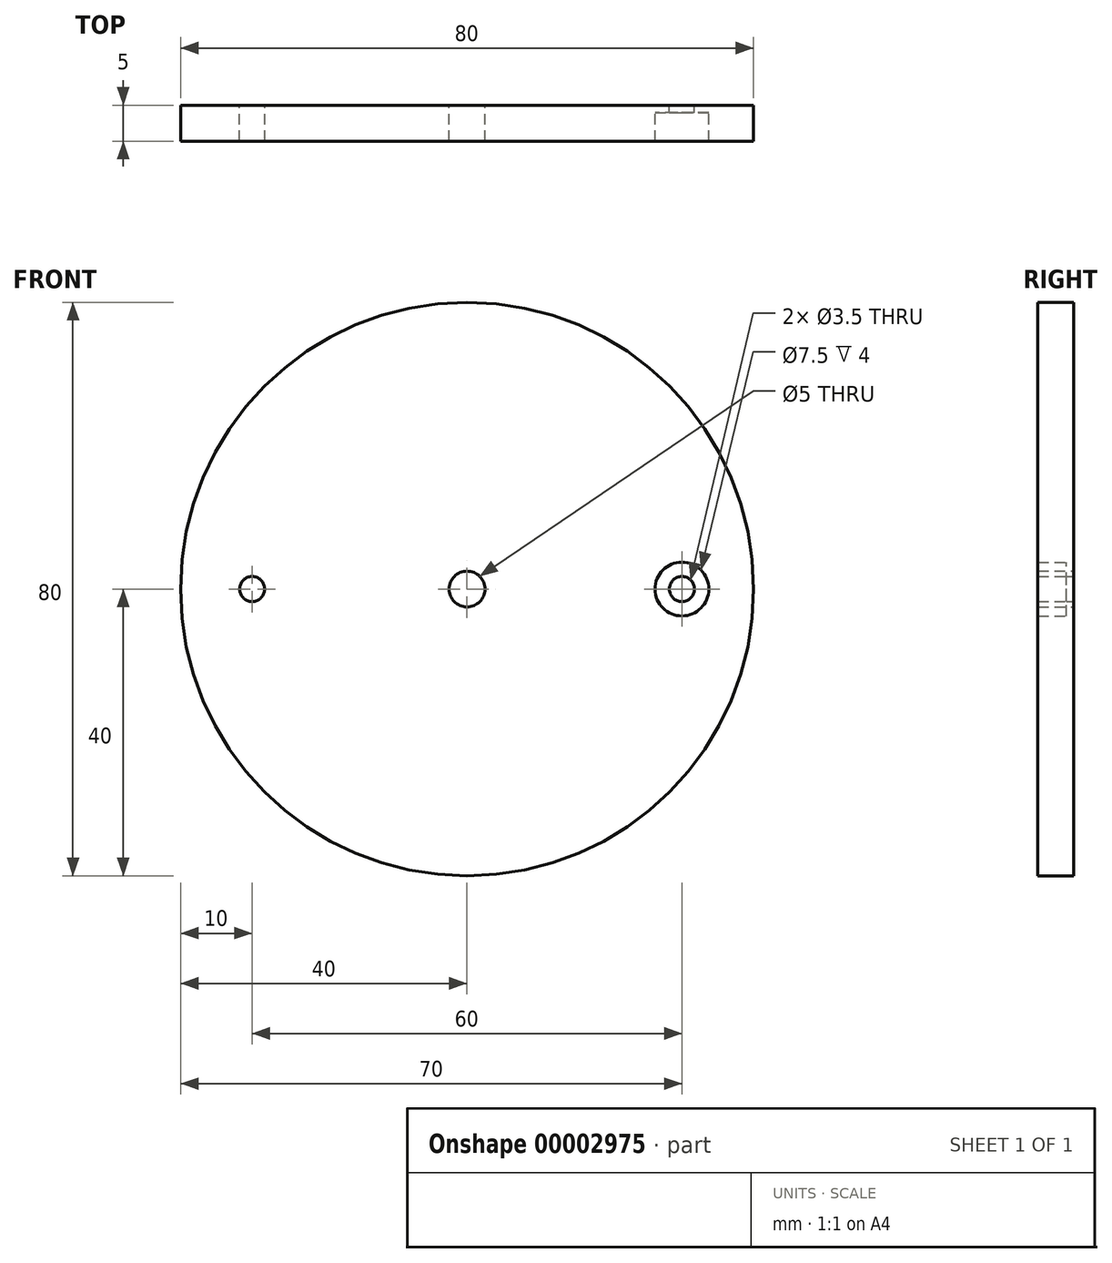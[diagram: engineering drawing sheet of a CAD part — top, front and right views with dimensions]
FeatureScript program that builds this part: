
annotation { "Feature Type Name" : "Feature", "Feature Type Description" : "" }
export const myFeature = defineFeature(function(context is Context, id is Id, definition is map)
    precondition{}
    {
        {
            var Q0;
            Q0=qCreatedBy(makeId("Front.planeOp"),FACE);
            var sketch = newSketch(context, id + "F0", { "sketchPlane" : qUnion([Q0])});
            skCircle(sketch, "E0", {"center": v(0, 0) * mm, "radius": 40 * mm});
            skCircle(sketch, "E1", {"center": v(-30, 0) * mm, "radius": 1.75 * mm});
            skCircle(sketch, "E2.0.MirrorC", {"center": v(30, 0) * mm, "radius": 1.75 * mm});
            skSolve(sketch);
        }
        {
            var Q0;
            Q0=makeQuery(id+"F0.imprint","IMPRINT",FACE,{"disambiguationData":[TD([[makeQuery(id+"F0.imprint","IMPRINT",EDGE,{"derivedFrom":sQuery(id+"F0.wireOp",EDGE,"E0")}),1.0]])]});
            extrude(context, id + "F1", {"entities" : qUnion([Q0]), "depth" : 1 * mm});
        }
        {
            var Q0;
            Q0=makeQuery(id+"F1.opExtrude","CAP_FACE",FACE,{"disambiguationData":[OSD([sQuery(id+"F0.wireOp",EDGE,"E0"),sQuery(id+"F0.wireOp",EDGE,"E1"),sQuery(id+"F0.wireOp",EDGE,"E2.0.MirrorC")])],"isStart":false});
            var sketch = newSketch(context, id + "F2", { "sketchPlane" : qUnion([Q0])});
            skCircle(sketch, "E3.0", {"center": v(-30, 0) * mm, "radius": 1.75 * mm});
            skCircle(sketch, "E4", {"center": v(-30, 0) * mm, "radius": 3.75 * mm});
            skCircle(sketch, "E5.0.MirrorC", {"center": v(30, 0) * mm, "radius": 3.75 * mm});
            skCircle(sketch, "E6.0.MirrorC", {"center": v(30, 0) * mm, "radius": 1.75 * mm});
            skSolve(sketch);
        }
        {
            var Q0;
            Q0=makeQuery(id+"F2.imprint","IMPRINT",FACE,{"disambiguationData":[TD([[makeQuery(id+"F2.imprint","IMPRINT",EDGE,{"derivedFrom":sQuery(id+"F2.wireOp",EDGE,"E3.0")}),-1.0]])]});
            var Q1;
            Q1=makeQuery(id+"F2.imprint","IMPRINT",FACE,{"disambiguationData":[TD([[makeQuery(id+"F2.imprint","IMPRINT",EDGE,{"derivedFrom":sQuery(id+"F2.wireOp",EDGE,"E5.0.MirrorC")}),-1.0]])]});
            extrude(context, id + "F3", {"entities" : qUnion([Q0, Q1]), "operationType" : NewBodyOperationType.ADD, "depth" : 4 * mm});
        }
        {
            var Q0;
            Q0=makeQuery(id+"F1.opExtrude","CAP_FACE",FACE,{"disambiguationData":[OSD([sQuery(id+"F0.wireOp",EDGE,"E0"),sQuery(id+"F0.wireOp",EDGE,"E1"),sQuery(id+"F0.wireOp",EDGE,"E2.0.MirrorC")])],"isStart":true});
            var sketch = newSketch(context, id + "F4", { "sketchPlane" : qUnion([Q0])});
            skCircle(sketch, "E7", {"center": v(0, 0) * mm, "radius": 2.5 * mm});
            skSolve(sketch);
        }
        {
            var Q0;
            Q0=makeQuery(id+"F1.opExtrude","CAP_FACE",FACE,{"disambiguationData":[OSD([sQuery(id+"F0.wireOp",EDGE,"E0"),sQuery(id+"F0.wireOp",EDGE,"E1"),sQuery(id+"F0.wireOp",EDGE,"E2.0.MirrorC")])],"isStart":false});
            var sketch = newSketch(context, id + "F5", { "sketchPlane" : qUnion([Q0])});
            skCircle(sketch, "E8.0", {"center": v(-30, 0) * mm, "radius": 3.75 * mm});
            skCircle(sketch, "E9.0", {"center": v(30, 0) * mm, "radius": 3.75 * mm});
            skLineSegment(sketch, "E10", {"start": v(-30, 3.75) * mm, "end": v(-30, -3.75) * mm, "construction": true});
            skLineSegment(sketch, "E11", {"start": v(30, 3.75) * mm, "end": v(30, -3.75) * mm, "construction": true});
            skLineSegment(sketch, "E12", {"start": v(-30, 3.75) * mm, "end": v(30, 3.75) * mm});
            skLineSegment(sketch, "E13", {"start": v(-30, -3.75) * mm, "end": v(30, -3.75) * mm});
            skSolve(sketch);
        }
        {
            var Q0;
            {var subQ1=sQuery(id+"F5.wireOp",EDGE,"E12");Q0=makeQuery(id+"F5.imprint","IMPRINT",FACE,{"disambiguationData":[TD([[makeQuery(id+"F5.imprint","IMPRINT",EDGE,{"derivedFrom":subQ1}),-1.0]])]});}
            var Q1;
            Q1=makeQuery(id+"F3.opExtrude","CAP_FACE",FACE,{"disambiguationData":[OSD([sQuery(id+"F2.wireOp",EDGE,"E3.0"),sQuery(id+"F2.wireOp",EDGE,"E4")])],"isStart":false});
            extrude(context, id + "F6", {"entities" : qUnion([Q0]), "operationType" : NewBodyOperationType.ADD, "endBound" : BoundingType.UP_TO_SURFACE, "endBoundEntityFace" : qUnion([Q1]), "depth" : 25 * mm});
        }
        {
            var Q0;
            Q0=makeQuery(id+"F4.imprint","IMPRINT",FACE,{"disambiguationData":[TD([[makeQuery(id+"F4.imprint","IMPRINT",EDGE,{"derivedFrom":sQuery(id+"F4.wireOp",EDGE,"E7")}),1.0]])]});
            extrude(context, id + "F7", {"entities" : qUnion([Q0]), "operationType" : NewBodyOperationType.REMOVE, "endBound" : BoundingType.THROUGH_ALL, "oppositeDirection" : true, "depth" : 25 * mm});
        }
    });
